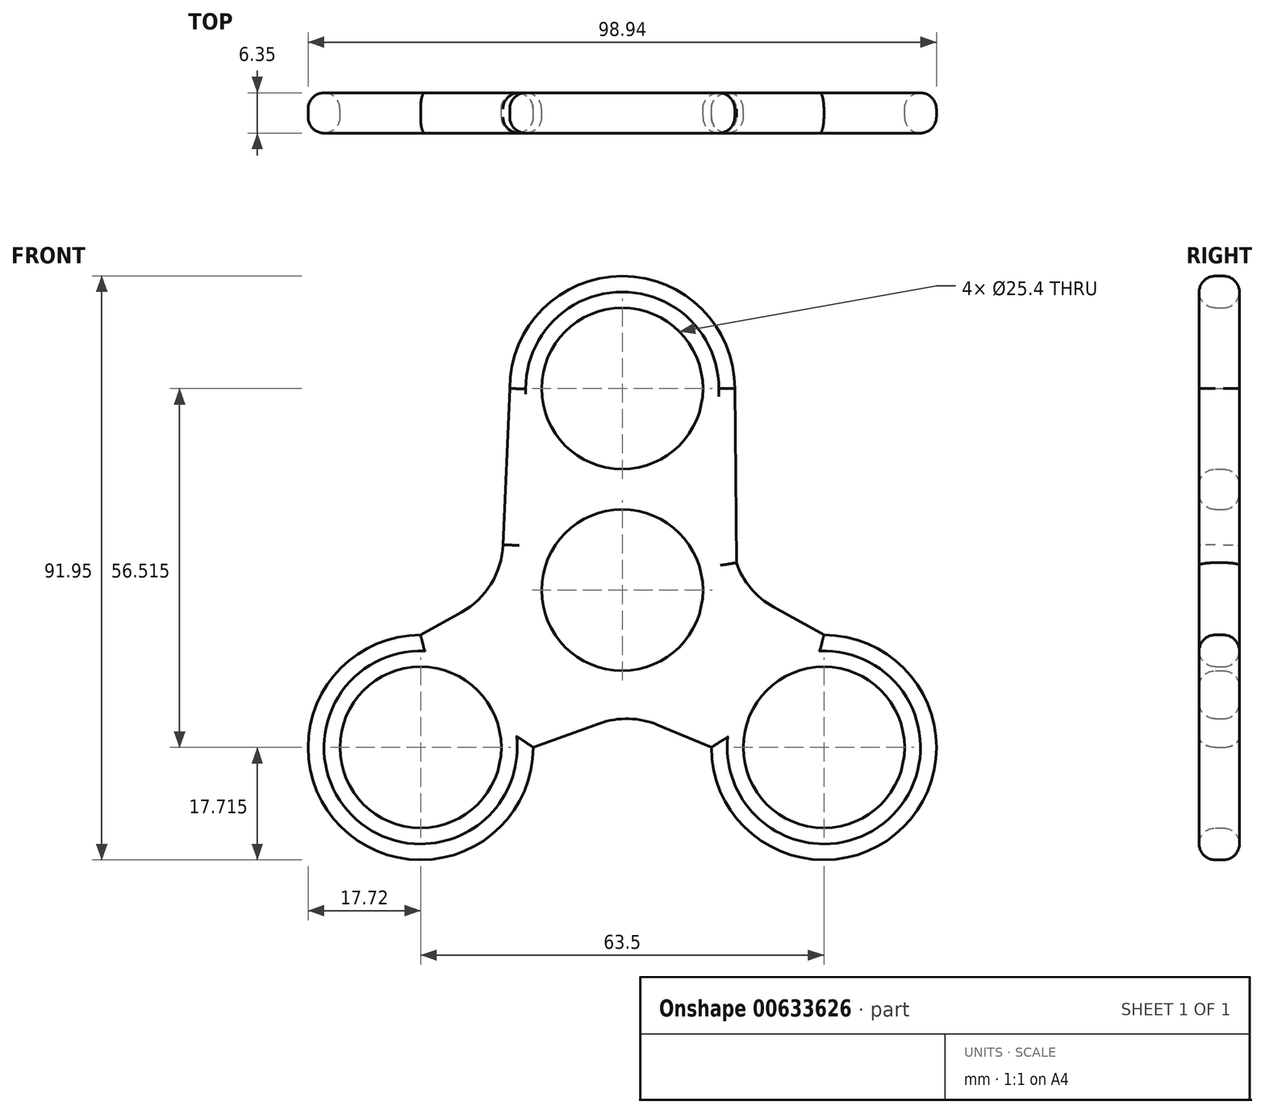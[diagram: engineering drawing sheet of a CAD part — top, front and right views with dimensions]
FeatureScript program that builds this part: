
annotation { "Feature Type Name" : "Feature", "Feature Type Description" : "" }
export const myFeature = defineFeature(function(context is Context, id is Id, definition is map)
    precondition{}
    {
        {
            var Q0;
            Q0=qCreatedBy(makeId("Front.planeOp"),FACE);
            var sketch = newSketch(context, id + "F0", { "sketchPlane" : qUnion([Q0])});
            skCircle(sketch, "E0", {"center": v(0, 0) * mm, "radius": 12.7 * mm});
            skCircle(sketch, "E1", {"center": v(-31.75, -24.77) * mm, "radius": 12.7 * mm});
            skCircle(sketch, "E2.MirrorC", {"center": v(31.75, -24.77) * mm, "radius": 12.7 * mm});
            skCircle(sketch, "E3", {"center": v(0, 31.75) * mm, "radius": 12.7 * mm});
            skArc(sketch, "E4", {"start": v(-31.75, -42.48) * mm, "mid": v(-44.28, -37.3) * mm, "end": v(-49.47, -24.77) * mm});
            skArc(sketch, "E5.MirrorCS", {"start": v(31.75, -42.48) * mm, "mid": v(44.28, -37.3) * mm, "end": v(49.47, -24.77) * mm});
            skLineSegment(sketch, "E6", {"start": v(-31.75, -24.77) * mm, "end": v(-31.75, -42.48) * mm, "construction": true});
            skArc(sketch, "E7.MirrorCS", {"start": v(-31.75, -42.48) * mm, "mid": v(-19.22, -37.3) * mm, "end": v(-14.03, -24.77) * mm});
            skArc(sketch, "E8.MirrorCS", {"start": v(31.75, -42.48) * mm, "mid": v(19.22, -37.3) * mm, "end": v(14.03, -24.77) * mm});
            skLineSegment(sketch, "E9", {"start": v(-31.75, -24.77) * mm, "end": v(-49.47, -24.77) * mm, "construction": true});
            skArc(sketch, "E10.MirrorCS", {"start": v(-31.75, -7.05) * mm, "mid": v(-44.28, -12.24) * mm, "end": v(-49.47, -24.77) * mm});
            skArc(sketch, "E11.MirrorCS", {"start": v(31.75, -7.05) * mm, "mid": v(44.28, -12.24) * mm, "end": v(49.47, -24.77) * mm});
            skArc(sketch, "E12", {"start": v(0, 49.47) * mm, "mid": v(-12.53, 44.28) * mm, "end": v(-17.72, 31.75) * mm});
            skArc(sketch, "E13.MirrorCS", {"start": v(0, 49.47) * mm, "mid": v(12.53, 44.28) * mm, "end": v(17.72, 31.75) * mm});
            skLineSegment(sketch, "E14", {"start": v(-17.72, 31.75) * mm, "end": v(17.72, 31.75) * mm, "construction": true});
            skLineSegment(sketch, "E15", {"start": v(-14.03, -24.77) * mm, "end": v(-3.58, -21) * mm});
            skLineSegment(sketch, "E16", {"start": v(5.63, -21.24) * mm, "end": v(14.03, -24.77) * mm});
            skPoint(sketch, "E17.visualSharp", {"position": v(1.07, -19.33) * mm});
            skArc(sketch, "E17.filletArc", {"start": v(5.63, -21.24) * mm, "mid": v(1.05, -20.26) * mm, "end": v(-3.58, -21) * mm});
            skLineSegment(sketch, "E18", {"start": v(-31.75, -7.05) * mm, "end": v(-25.3, -3.47) * mm});
            skLineSegment(sketch, "E19", {"start": v(23.8, -2.64) * mm, "end": v(31.75, -7.05) * mm});
            skPoint(sketch, "E20.visualSharp", {"position": v(-19.05, 0) * mm});
            skArc(sketch, "E20.filletArc", {"start": v(-25.3, -3.47) * mm, "mid": v(-20.65, 0.98) * mm, "end": v(-18.78, 7.15) * mm});
            skPoint(sketch, "E21.visualSharp", {"position": v(19.05, 0) * mm});
            skArc(sketch, "E21.filletArc", {"start": v(17.97, 4.32) * mm, "mid": v(20.24, 0.3) * mm, "end": v(23.8, -2.64) * mm});
            skLineSegment(sketch, "E22", {"start": v(-18.78, 7.15) * mm, "end": v(-17.72, 31.75) * mm});
            skLineSegment(sketch, "E23", {"start": v(17.72, 31.75) * mm, "end": v(17.97, 4.32) * mm});
            skSolve(sketch);
        }
        {
            var Q0;
            Q0 = qSketchRegion(id + "F0", true);
            extrude(context, id + "F1", {"entities" : qUnion([Q0]), "depth" : 6.35 * mm, "offsetDistance" : 25.4 * mm});
        }
        {
            var Q0;
            Q0=makeQuery(id+"F1.opExtrude","CAP_FACE",FACE,{"disambiguationData":[OSD([sQuery(id+"F0.wireOp",EDGE,"E0"),sQuery(id+"F0.wireOp",EDGE,"E1"),sQuery(id+"F0.wireOp",EDGE,"E2.MirrorC"),sQuery(id+"F0.wireOp",EDGE,"E3"),sQuery(id+"F0.wireOp",EDGE,"E4"),sQuery(id+"F0.wireOp",EDGE,"E5.MirrorCS"),sQuery(id+"F0.wireOp",EDGE,"E7.MirrorCS"),sQuery(id+"F0.wireOp",EDGE,"E8.MirrorCS"),sQuery(id+"F0.wireOp",EDGE,"E10.MirrorCS"),sQuery(id+"F0.wireOp",EDGE,"E11.MirrorCS"),sQuery(id+"F0.wireOp",EDGE,"E12"),sQuery(id+"F0.wireOp",EDGE,"E13.MirrorCS"),sQuery(id+"F0.wireOp",EDGE,"E15"),sQuery(id+"F0.wireOp",EDGE,"E16"),sQuery(id+"F0.wireOp",EDGE,"E17.filletArc"),sQuery(id+"F0.wireOp",EDGE,"E18"),sQuery(id+"F0.wireOp",EDGE,"YQhEMSOv-0u2h-00uE-mmgK-wasKY4ADhsX0"),sQuery(id+"F0.wireOp",EDGE,"YXcXhWem-3ha5-BN11-eKB1-WLZeE76oCgJG"),sQuery(id+"F0.wireOp",EDGE,"E19"),sQuery(id+"F0.wireOp",EDGE,"E20.filletArc"),sQuery(id+"F0.wireOp",EDGE,"E21.filletArc")])],"isStart":false});
            var Q1;
            Q1=makeQuery(id+"F1.opExtrude","CAP_FACE",FACE,{"disambiguationData":[OSD([sQuery(id+"F0.wireOp",EDGE,"E0"),sQuery(id+"F0.wireOp",EDGE,"E1"),sQuery(id+"F0.wireOp",EDGE,"E2.MirrorC"),sQuery(id+"F0.wireOp",EDGE,"E3"),sQuery(id+"F0.wireOp",EDGE,"E4"),sQuery(id+"F0.wireOp",EDGE,"E5.MirrorCS"),sQuery(id+"F0.wireOp",EDGE,"E7.MirrorCS"),sQuery(id+"F0.wireOp",EDGE,"E8.MirrorCS"),sQuery(id+"F0.wireOp",EDGE,"E10.MirrorCS"),sQuery(id+"F0.wireOp",EDGE,"E11.MirrorCS"),sQuery(id+"F0.wireOp",EDGE,"E12"),sQuery(id+"F0.wireOp",EDGE,"E13.MirrorCS"),sQuery(id+"F0.wireOp",EDGE,"E15"),sQuery(id+"F0.wireOp",EDGE,"E16"),sQuery(id+"F0.wireOp",EDGE,"E17.filletArc"),sQuery(id+"F0.wireOp",EDGE,"E18"),sQuery(id+"F0.wireOp",EDGE,"YQhEMSOv-0u2h-00uE-mmgK-wasKY4ADhsX0"),sQuery(id+"F0.wireOp",EDGE,"YXcXhWem-3ha5-BN11-eKB1-WLZeE76oCgJG"),sQuery(id+"F0.wireOp",EDGE,"E19"),sQuery(id+"F0.wireOp",EDGE,"E20.filletArc"),sQuery(id+"F0.wireOp",EDGE,"E21.filletArc")])],"isStart":true});
            fillet(context, id + "F2", {"entities" : qUnion([Q0, Q1]), "radius" : 2.54 * mm, "tangentPropagation" : true, "allowEdgeOverflow" : false});
        }
    });
